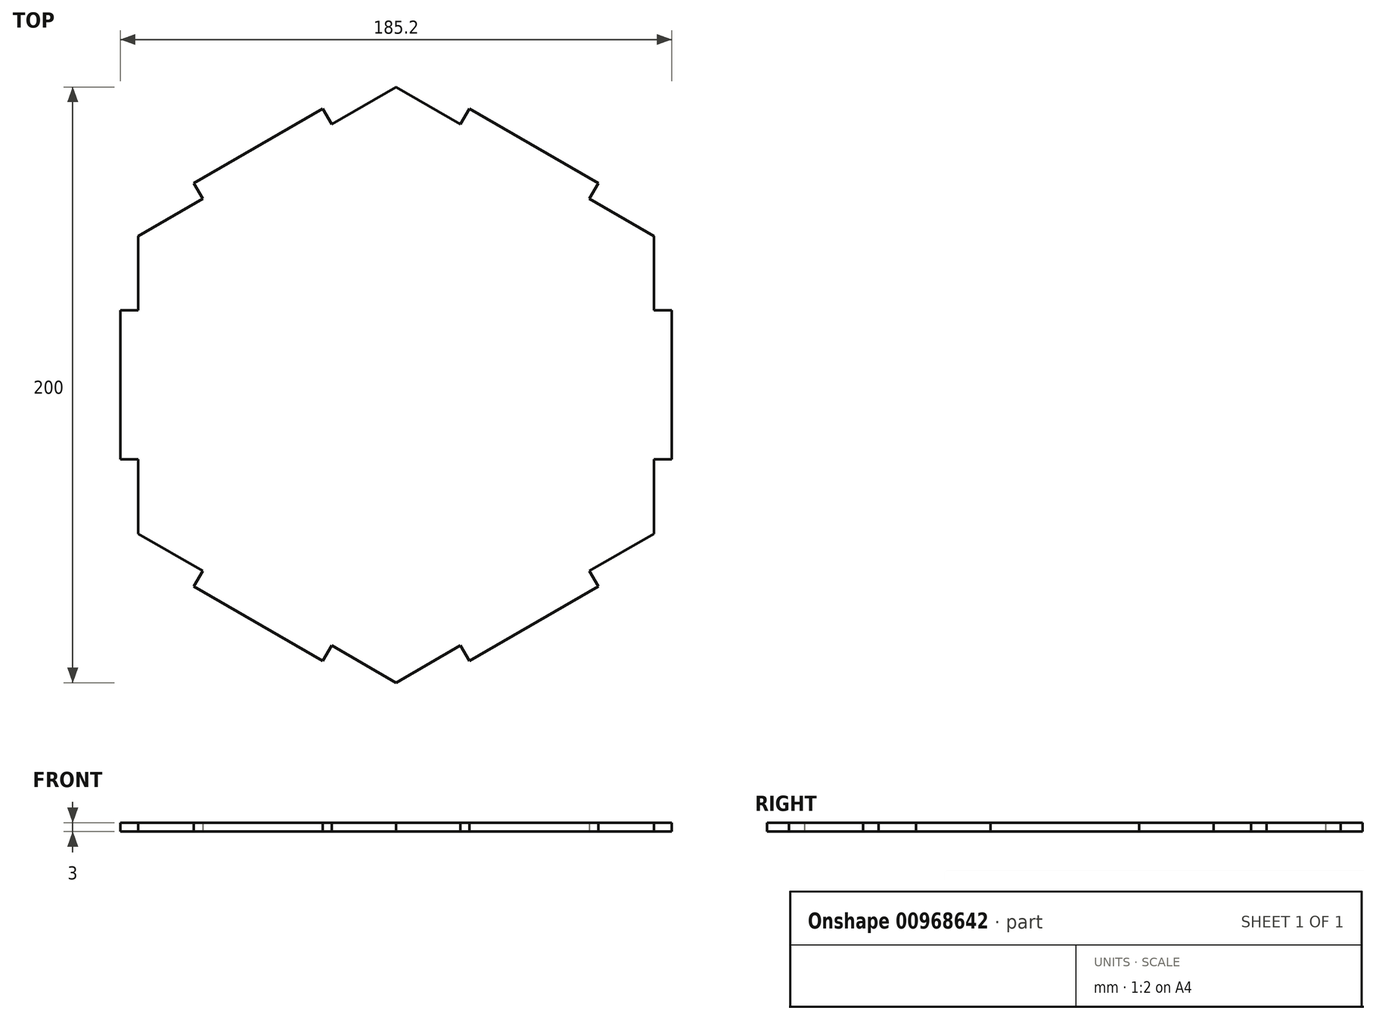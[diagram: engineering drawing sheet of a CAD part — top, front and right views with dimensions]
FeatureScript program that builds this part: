
annotation { "Feature Type Name" : "Feature", "Feature Type Description" : "" }
export const myFeature = defineFeature(function(context is Context, id is Id, definition is map)
    precondition{}
    {
        {
            var Q0;
            Q0=qCreatedBy(makeId("Top.planeOp"),FACE);
            var sketch = newSketch(context, id + "F0", { "sketchPlane" : qUnion([Q0])});
            skCircle(sketch, "E0.cCircle", {"center": v(0, 0) * mm, "radius": 100 * mm, "construction": true});
            skLineSegment(sketch, "E0.0", {"start": v(0, -100) * mm, "end": v(-21.65, -87.5) * mm});
            skLineSegment(sketch, "E0.1", {"start": v(-86.6, -50) * mm, "end": v(-86.6, -25) * mm});
            skLineSegment(sketch, "E0.2", {"start": v(-86.6, 50) * mm, "end": v(-64.95, 62.5) * mm});
            skLineSegment(sketch, "E0.3", {"start": v(0, 100) * mm, "end": v(21.65, 87.5) * mm});
            skLineSegment(sketch, "E0.4", {"start": v(86.6, 50) * mm, "end": v(86.6, 25) * mm});
            skLineSegment(sketch, "E0.5", {"start": v(86.6, -50) * mm, "end": v(64.95, -62.5) * mm});
            skLineSegment(sketch, "E1", {"start": v(86.6, 25) * mm, "end": v(92.6, 25) * mm});
            skLineSegment(sketch, "E2", {"start": v(92.6, 25) * mm, "end": v(92.6, -25) * mm});
            skLineSegment(sketch, "E3", {"start": v(92.6, -25) * mm, "end": v(86.6, -25) * mm});
            skLineSegment(sketch, "E4.trimOffspring", {"start": v(86.6, -25) * mm, "end": v(86.6, -50) * mm});
            skLineSegment(sketch, "E5.1.0", {"start": v(24.65, 92.7) * mm, "end": v(67.95, 67.7) * mm});
            skLineSegment(sketch, "E5.1.1", {"start": v(21.65, 87.5) * mm, "end": v(24.65, 92.7) * mm});
            skLineSegment(sketch, "E5.1.2", {"start": v(67.95, 67.7) * mm, "end": v(64.95, 62.5) * mm});
            skLineSegment(sketch, "E5.2.0", {"start": v(-67.95, 67.7) * mm, "end": v(-24.65, 92.7) * mm});
            skLineSegment(sketch, "E5.2.1", {"start": v(-64.95, 62.5) * mm, "end": v(-67.95, 67.7) * mm});
            skLineSegment(sketch, "E5.2.2", {"start": v(-24.65, 92.7) * mm, "end": v(-21.65, 87.5) * mm});
            skLineSegment(sketch, "E5.3.0", {"start": v(-92.6, -25) * mm, "end": v(-92.6, 25) * mm});
            skLineSegment(sketch, "E5.3.1", {"start": v(-86.6, -25) * mm, "end": v(-92.6, -25) * mm});
            skLineSegment(sketch, "E5.3.2", {"start": v(-92.6, 25) * mm, "end": v(-86.6, 25) * mm});
            skLineSegment(sketch, "E5.4.0", {"start": v(-24.65, -92.7) * mm, "end": v(-67.95, -67.7) * mm});
            skLineSegment(sketch, "E5.4.1", {"start": v(-21.65, -87.5) * mm, "end": v(-24.65, -92.7) * mm});
            skLineSegment(sketch, "E5.4.2", {"start": v(-67.95, -67.7) * mm, "end": v(-64.95, -62.5) * mm});
            skLineSegment(sketch, "E5.5.0", {"start": v(67.95, -67.7) * mm, "end": v(24.65, -92.7) * mm});
            skLineSegment(sketch, "E5.5.1", {"start": v(64.95, -62.5) * mm, "end": v(67.95, -67.7) * mm});
            skLineSegment(sketch, "E5.5.2", {"start": v(24.65, -92.7) * mm, "end": v(21.65, -87.5) * mm});
            skLineSegment(sketch, "E6.trimOffspring", {"start": v(21.65, -87.5) * mm, "end": v(0, -100) * mm});
            skLineSegment(sketch, "E7.trimOffspring", {"start": v(64.95, 62.5) * mm, "end": v(86.6, 50) * mm});
            skLineSegment(sketch, "E8.trimOffspring", {"start": v(-21.65, 87.5) * mm, "end": v(0, 100) * mm});
            skLineSegment(sketch, "E9.trimOffspring", {"start": v(-86.6, 25) * mm, "end": v(-86.6, 50) * mm});
            skLineSegment(sketch, "E10.trimOffspring", {"start": v(-64.95, -62.5) * mm, "end": v(-86.6, -50) * mm});
            skSolve(sketch);
        }
        {
            var Q0;
            Q0=makeQuery(id+"F0.imprint","IMPRINT",FACE,{"disambiguationData":[TD([[makeQuery(id+"F0.imprint","IMPRINT",EDGE,{"derivedFrom":sQuery(id+"F0.wireOp",EDGE,"E0.0")}),-1.0]])]});
            extrude(context, id + "F1", {"entities" : qUnion([Q0]), "depth" : 3 * mm, "offsetDistance" : 25 * mm});
        }
    });
